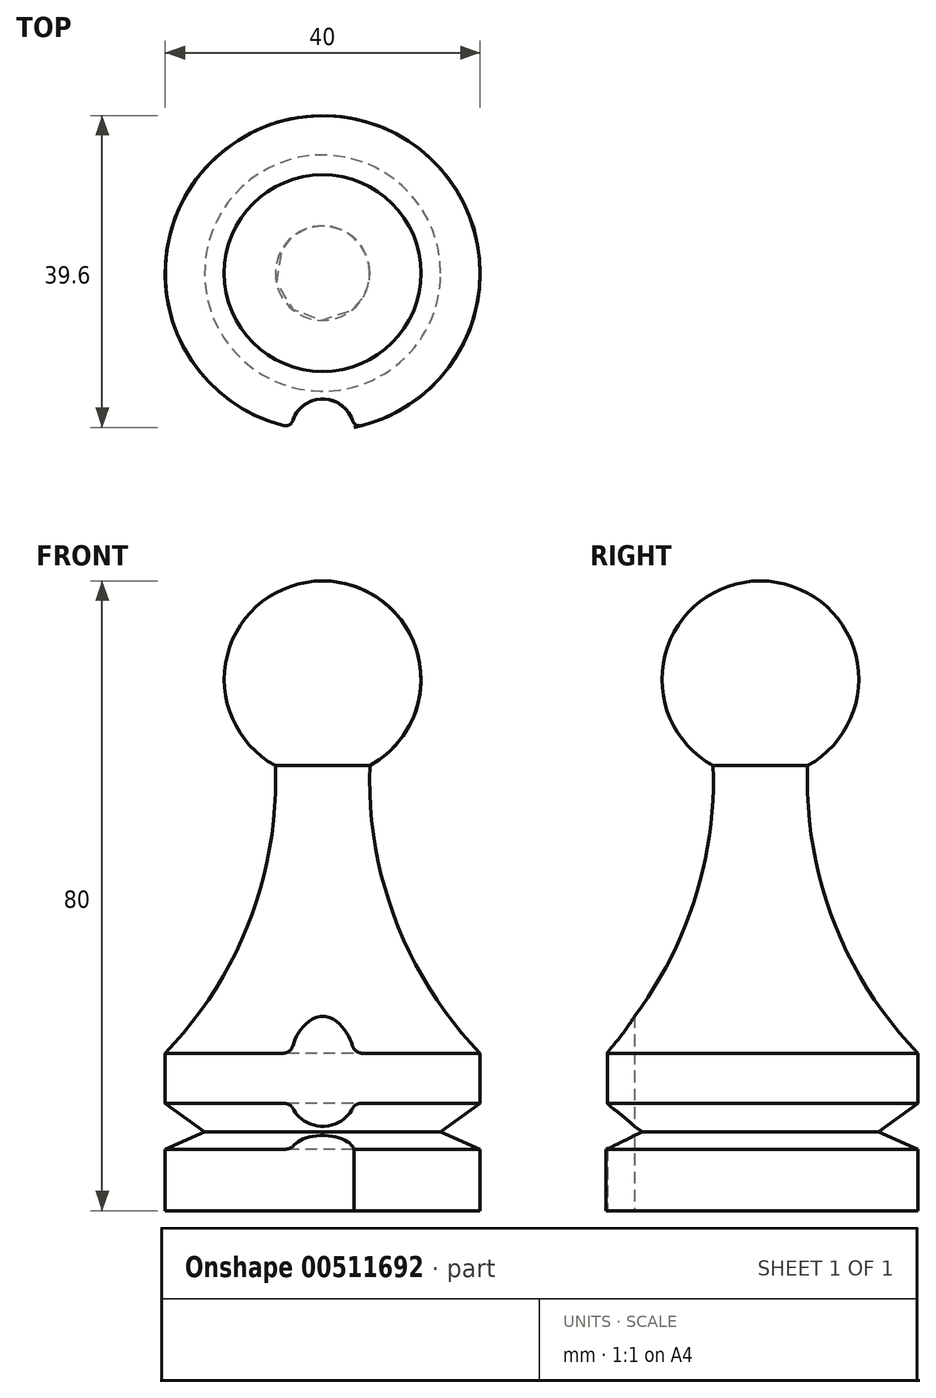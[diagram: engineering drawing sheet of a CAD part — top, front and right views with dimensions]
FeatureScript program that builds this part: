
annotation { "Feature Type Name" : "Feature", "Feature Type Description" : "" }
export const myFeature = defineFeature(function(context is Context, id is Id, definition is map)
    precondition{}
    {
        {
            var Q0;
            Q0=qCreatedBy(makeId("Front.planeOp"),FACE);
            var sketch = newSketch(context, id + "F0", { "sketchPlane" : qUnion([Q0])});
            skLineSegment(sketch, "E0", {"start": v(0, 53.24) * mm, "end": v(0, -26.76) * mm, "construction": true});
            skLineSegment(sketch, "E1", {"start": v(0, -26.76) * mm, "end": v(20, -26.76) * mm});
            skLineSegment(sketch, "E2", {"start": v(20, -26.76) * mm, "end": v(20, -18.97) * mm});
            skLineSegment(sketch, "E3", {"start": v(20, -18.97) * mm, "end": v(15, -16.76) * mm});
            skLineSegment(sketch, "E4", {"start": v(15, -16.76) * mm, "end": v(20, -13.11) * mm});
            skLineSegment(sketch, "E5", {"start": v(20, -13.11) * mm, "end": v(20, -6.76) * mm});
            skArc(sketch, "E6", {"start": v(6, 29.78) * mm, "mid": v(9.28, 10.08) * mm, "end": v(20, -6.76) * mm});
            skArc(sketch, "E7", {"start": v(6, 29.78) * mm, "mid": v(12.11, 43.84) * mm, "end": v(0, 53.24) * mm});
            skLineSegment(sketch, "E8", {"start": v(0, 53.24) * mm, "end": v(0, -26.76) * mm});
            skSolve(sketch);
        }
        {
            var Q0;
            Q0 = qSketchRegion(id + "F0", true);
            var Q1;
            Q1=sQuery(id+"F0.wireOp",EDGE,"E8");
            revolve(context, id + "F1", {"entities" : qUnion([Q0]), "axis" : qUnion([Q1]), "revolveType" : RevolveType.FULL});
        }
        {
            var Q0;
            Q0=makeQuery(id+"F1.opRevolve","SWEPT_FACE",FACE,{"disambiguationData":[OSD([sQuery(id+"F0.wireOp",EDGE,"E1")])]});
            var sketch = newSketch(context, id + "F2", { "sketchPlane" : qUnion([Q0])});
            skCircle(sketch, "E9", {"center": v(0, 20) * mm, "radius": 4 * mm});
            skSolve(sketch);
        }
        {
            var Q0;
            Q0 = qSketchRegion(id + "F2", true);
            extrude(context, id + "F3", {"entities" : qUnion([Q0]), "operationType" : NewBodyOperationType.REMOVE, "oppositeDirection" : true, "depth" : 25 * mm, "offsetDistance" : 25 * mm});
        }
        {
            var Q0;
            {var subQ0=sQuery(id+"F2.wireOp",EDGE,"E9");var subQ1=makeQuery(id+"F1.opRevolve","SWEPT_FACE",FACE,{"disambiguationData":[OSD([sQuery(id+"F0.wireOp",EDGE,"E4")])]});var subQ3=makeQuery(id+"F1.opRevolve","SWEPT_FACE",FACE,{"disambiguationData":[OSD([sQuery(id+"F0.wireOp",EDGE,"E5")])]});var subQ4=makeQuery(id+"F3.boolean.opBoolean","COPY",FACE,{"disambiguationData":[TD([subQ1])],"derivedFrom":makeQuery(id+"F3.opExtrude","SWEPT_FACE",FACE,{"disambiguationData":[OSD([subQ0])]})});Q0=makeQuery(id+"FM0jg12cZnN2cx2_1.5.F3.boolean.opBoolean","INTERSECT",EDGE,{"disambiguationData":[OD(0.0)],"derivedFrom":[makeQuery(id+"FM0jg12cZnN2cx2_1.4.F3.boolean.opBoolean","SPLIT",FACE,{"disambiguationData":[TD([subQ4])],"derivedFrom":makeQuery(id+"FM0jg12cZnN2cx2_1.3.F3.boolean.opBoolean","SPLIT",FACE,{"disambiguationData":[TD([subQ4])],"derivedFrom":makeQuery(id+"FM0jg12cZnN2cx2_1.2.F3.boolean.opBoolean","SPLIT",FACE,{"disambiguationData":[TD([subQ4])],"derivedFrom":makeQuery(id+"FM0jg12cZnN2cx2_1.1.F3.boolean.opBoolean","SPLIT",FACE,{"disambiguationData":[OD(1.0)],"derivedFrom":subQ3})})})}),makeQuery(id+"FM0jg12cZnN2cx2_1.5.F3.opExtrude","SWEPT_FACE",FACE,{"disambiguationData":[OSD([subQ0])]})]});}
            var Q1;
            {var subQ0=sQuery(id+"F2.wireOp",EDGE,"E9");var subQ1=makeQuery(id+"F1.opRevolve","SWEPT_FACE",FACE,{"disambiguationData":[OSD([sQuery(id+"F0.wireOp",EDGE,"E4")])]});var subQ3=makeQuery(id+"F1.opRevolve","SWEPT_FACE",FACE,{"disambiguationData":[OSD([sQuery(id+"F0.wireOp",EDGE,"E5")])]});var subQ4=makeQuery(id+"F3.boolean.opBoolean","COPY",FACE,{"disambiguationData":[TD([subQ1])],"derivedFrom":makeQuery(id+"F3.opExtrude","SWEPT_FACE",FACE,{"disambiguationData":[OSD([subQ0])]})});Q1=makeQuery(id+"FM0jg12cZnN2cx2_1.5.F3.boolean.opBoolean","INTERSECT",EDGE,{"disambiguationData":[OD(1.0)],"derivedFrom":[makeQuery(id+"FM0jg12cZnN2cx2_1.4.F3.boolean.opBoolean","SPLIT",FACE,{"disambiguationData":[TD([subQ4])],"derivedFrom":makeQuery(id+"FM0jg12cZnN2cx2_1.3.F3.boolean.opBoolean","SPLIT",FACE,{"disambiguationData":[TD([subQ4])],"derivedFrom":makeQuery(id+"FM0jg12cZnN2cx2_1.2.F3.boolean.opBoolean","SPLIT",FACE,{"disambiguationData":[TD([subQ4])],"derivedFrom":makeQuery(id+"FM0jg12cZnN2cx2_1.1.F3.boolean.opBoolean","SPLIT",FACE,{"disambiguationData":[OD(1.0)],"derivedFrom":subQ3})})})}),makeQuery(id+"FM0jg12cZnN2cx2_1.5.F3.opExtrude","SWEPT_FACE",FACE,{"disambiguationData":[OSD([subQ0])]})]});}
            var Q2;
            {var subQ0=sQuery(id+"F2.wireOp",EDGE,"E9");var subQ1=makeQuery(id+"F1.opRevolve","SWEPT_FACE",FACE,{"disambiguationData":[OSD([sQuery(id+"F0.wireOp",EDGE,"E1")])]});var subQ2=makeQuery(id+"F1.opRevolve","SWEPT_FACE",FACE,{"disambiguationData":[OSD([sQuery(id+"F0.wireOp",EDGE,"E2")])]});var subQ4=makeQuery(id+"F3.boolean.opBoolean","COPY",FACE,{"disambiguationData":[TD([subQ1])],"derivedFrom":makeQuery(id+"F3.opExtrude","SWEPT_FACE",FACE,{"disambiguationData":[OSD([subQ0])]})});Q2=makeQuery(id+"FM0jg12cZnN2cx2_1.5.F3.boolean.opBoolean","INTERSECT",EDGE,{"disambiguationData":[OD(0.0)],"derivedFrom":[makeQuery(id+"FM0jg12cZnN2cx2_1.4.F3.boolean.opBoolean","SPLIT",FACE,{"disambiguationData":[TD([subQ4])],"derivedFrom":makeQuery(id+"FM0jg12cZnN2cx2_1.3.F3.boolean.opBoolean","SPLIT",FACE,{"disambiguationData":[TD([subQ4])],"derivedFrom":makeQuery(id+"FM0jg12cZnN2cx2_1.2.F3.boolean.opBoolean","SPLIT",FACE,{"disambiguationData":[TD([subQ4])],"derivedFrom":makeQuery(id+"FM0jg12cZnN2cx2_1.1.F3.boolean.opBoolean","SPLIT",FACE,{"disambiguationData":[OD(1.0)],"derivedFrom":subQ2})})})}),makeQuery(id+"FM0jg12cZnN2cx2_1.5.F3.opExtrude","SWEPT_FACE",FACE,{"disambiguationData":[OSD([subQ0])]})]});}
            var Q3;
            {var subQ0=sQuery(id+"F2.wireOp",EDGE,"E9");var subQ1=makeQuery(id+"F1.opRevolve","SWEPT_FACE",FACE,{"disambiguationData":[OSD([sQuery(id+"F0.wireOp",EDGE,"E1")])]});var subQ2=makeQuery(id+"F1.opRevolve","SWEPT_FACE",FACE,{"disambiguationData":[OSD([sQuery(id+"F0.wireOp",EDGE,"E2")])]});var subQ4=makeQuery(id+"F3.boolean.opBoolean","COPY",FACE,{"disambiguationData":[TD([subQ1])],"derivedFrom":makeQuery(id+"F3.opExtrude","SWEPT_FACE",FACE,{"disambiguationData":[OSD([subQ0])]})});Q3=makeQuery(id+"FM0jg12cZnN2cx2_1.5.F3.boolean.opBoolean","INTERSECT",EDGE,{"disambiguationData":[OD(1.0)],"derivedFrom":[makeQuery(id+"FM0jg12cZnN2cx2_1.4.F3.boolean.opBoolean","SPLIT",FACE,{"disambiguationData":[TD([subQ4])],"derivedFrom":makeQuery(id+"FM0jg12cZnN2cx2_1.3.F3.boolean.opBoolean","SPLIT",FACE,{"disambiguationData":[TD([subQ4])],"derivedFrom":makeQuery(id+"FM0jg12cZnN2cx2_1.2.F3.boolean.opBoolean","SPLIT",FACE,{"disambiguationData":[TD([subQ4])],"derivedFrom":makeQuery(id+"FM0jg12cZnN2cx2_1.1.F3.boolean.opBoolean","SPLIT",FACE,{"disambiguationData":[OD(1.0)],"derivedFrom":subQ2})})})}),makeQuery(id+"FM0jg12cZnN2cx2_1.5.F3.opExtrude","SWEPT_FACE",FACE,{"disambiguationData":[OSD([subQ0])]})]});}
            var Q4;
            {var subQ0=sQuery(id+"F2.wireOp",EDGE,"E9");var subQ1=makeQuery(id+"F1.opRevolve","SWEPT_FACE",FACE,{"disambiguationData":[OSD([sQuery(id+"F0.wireOp",EDGE,"E4")])]});var subQ3=makeQuery(id+"F1.opRevolve","SWEPT_FACE",FACE,{"disambiguationData":[OSD([sQuery(id+"F0.wireOp",EDGE,"E5")])]});var subQ4=makeQuery(id+"F3.boolean.opBoolean","COPY",FACE,{"disambiguationData":[TD([subQ1])],"derivedFrom":makeQuery(id+"F3.opExtrude","SWEPT_FACE",FACE,{"disambiguationData":[OSD([subQ0])]})});Q4=makeQuery(id+"FM0jg12cZnN2cx2_1.4.F3.boolean.opBoolean","INTERSECT",EDGE,{"disambiguationData":[OD(0.0)],"derivedFrom":[makeQuery(id+"FM0jg12cZnN2cx2_1.3.F3.boolean.opBoolean","SPLIT",FACE,{"disambiguationData":[TD([subQ4])],"derivedFrom":makeQuery(id+"FM0jg12cZnN2cx2_1.2.F3.boolean.opBoolean","SPLIT",FACE,{"disambiguationData":[TD([subQ4])],"derivedFrom":makeQuery(id+"FM0jg12cZnN2cx2_1.1.F3.boolean.opBoolean","SPLIT",FACE,{"disambiguationData":[OD(1.0)],"derivedFrom":subQ3})})}),makeQuery(id+"FM0jg12cZnN2cx2_1.4.F3.opExtrude","SWEPT_FACE",FACE,{"disambiguationData":[OSD([subQ0])]})]});}
            var Q5;
            {var subQ0=sQuery(id+"F2.wireOp",EDGE,"E9");var subQ1=makeQuery(id+"F1.opRevolve","SWEPT_FACE",FACE,{"disambiguationData":[OSD([sQuery(id+"F0.wireOp",EDGE,"E4")])]});var subQ3=makeQuery(id+"F1.opRevolve","SWEPT_FACE",FACE,{"disambiguationData":[OSD([sQuery(id+"F0.wireOp",EDGE,"E5")])]});var subQ4=makeQuery(id+"F3.boolean.opBoolean","COPY",FACE,{"disambiguationData":[TD([subQ1])],"derivedFrom":makeQuery(id+"F3.opExtrude","SWEPT_FACE",FACE,{"disambiguationData":[OSD([subQ0])]})});Q5=makeQuery(id+"FM0jg12cZnN2cx2_1.4.F3.boolean.opBoolean","INTERSECT",EDGE,{"disambiguationData":[OD(1.0)],"derivedFrom":[makeQuery(id+"FM0jg12cZnN2cx2_1.3.F3.boolean.opBoolean","SPLIT",FACE,{"disambiguationData":[TD([subQ4])],"derivedFrom":makeQuery(id+"FM0jg12cZnN2cx2_1.2.F3.boolean.opBoolean","SPLIT",FACE,{"disambiguationData":[TD([subQ4])],"derivedFrom":makeQuery(id+"FM0jg12cZnN2cx2_1.1.F3.boolean.opBoolean","SPLIT",FACE,{"disambiguationData":[OD(1.0)],"derivedFrom":subQ3})})}),makeQuery(id+"FM0jg12cZnN2cx2_1.4.F3.opExtrude","SWEPT_FACE",FACE,{"disambiguationData":[OSD([subQ0])]})]});}
            var Q6;
            {var subQ0=sQuery(id+"F2.wireOp",EDGE,"E9");var subQ1=makeQuery(id+"F1.opRevolve","SWEPT_FACE",FACE,{"disambiguationData":[OSD([sQuery(id+"F0.wireOp",EDGE,"E1")])]});var subQ2=makeQuery(id+"F1.opRevolve","SWEPT_FACE",FACE,{"disambiguationData":[OSD([sQuery(id+"F0.wireOp",EDGE,"E2")])]});var subQ4=makeQuery(id+"F3.boolean.opBoolean","COPY",FACE,{"disambiguationData":[TD([subQ1])],"derivedFrom":makeQuery(id+"F3.opExtrude","SWEPT_FACE",FACE,{"disambiguationData":[OSD([subQ0])]})});Q6=makeQuery(id+"FM0jg12cZnN2cx2_1.4.F3.boolean.opBoolean","INTERSECT",EDGE,{"disambiguationData":[OD(0.0)],"derivedFrom":[makeQuery(id+"FM0jg12cZnN2cx2_1.3.F3.boolean.opBoolean","SPLIT",FACE,{"disambiguationData":[TD([subQ4])],"derivedFrom":makeQuery(id+"FM0jg12cZnN2cx2_1.2.F3.boolean.opBoolean","SPLIT",FACE,{"disambiguationData":[TD([subQ4])],"derivedFrom":makeQuery(id+"FM0jg12cZnN2cx2_1.1.F3.boolean.opBoolean","SPLIT",FACE,{"disambiguationData":[OD(1.0)],"derivedFrom":subQ2})})}),makeQuery(id+"FM0jg12cZnN2cx2_1.4.F3.opExtrude","SWEPT_FACE",FACE,{"disambiguationData":[OSD([subQ0])]})]});}
            var Q7;
            {var subQ0=sQuery(id+"F2.wireOp",EDGE,"E9");var subQ1=makeQuery(id+"F1.opRevolve","SWEPT_FACE",FACE,{"disambiguationData":[OSD([sQuery(id+"F0.wireOp",EDGE,"E1")])]});var subQ2=makeQuery(id+"F1.opRevolve","SWEPT_FACE",FACE,{"disambiguationData":[OSD([sQuery(id+"F0.wireOp",EDGE,"E2")])]});var subQ4=makeQuery(id+"F3.boolean.opBoolean","COPY",FACE,{"disambiguationData":[TD([subQ1])],"derivedFrom":makeQuery(id+"F3.opExtrude","SWEPT_FACE",FACE,{"disambiguationData":[OSD([subQ0])]})});Q7=makeQuery(id+"FM0jg12cZnN2cx2_1.4.F3.boolean.opBoolean","INTERSECT",EDGE,{"disambiguationData":[OD(1.0)],"derivedFrom":[makeQuery(id+"FM0jg12cZnN2cx2_1.3.F3.boolean.opBoolean","SPLIT",FACE,{"disambiguationData":[TD([subQ4])],"derivedFrom":makeQuery(id+"FM0jg12cZnN2cx2_1.2.F3.boolean.opBoolean","SPLIT",FACE,{"disambiguationData":[TD([subQ4])],"derivedFrom":makeQuery(id+"FM0jg12cZnN2cx2_1.1.F3.boolean.opBoolean","SPLIT",FACE,{"disambiguationData":[OD(1.0)],"derivedFrom":subQ2})})}),makeQuery(id+"FM0jg12cZnN2cx2_1.4.F3.opExtrude","SWEPT_FACE",FACE,{"disambiguationData":[OSD([subQ0])]})]});}
            var Q8;
            {var subQ0=sQuery(id+"F2.wireOp",EDGE,"E9");var subQ1=makeQuery(id+"F1.opRevolve","SWEPT_FACE",FACE,{"disambiguationData":[OSD([sQuery(id+"F0.wireOp",EDGE,"E4")])]});var subQ3=makeQuery(id+"F1.opRevolve","SWEPT_FACE",FACE,{"disambiguationData":[OSD([sQuery(id+"F0.wireOp",EDGE,"E5")])]});var subQ4=makeQuery(id+"F3.boolean.opBoolean","COPY",FACE,{"disambiguationData":[TD([subQ1])],"derivedFrom":makeQuery(id+"F3.opExtrude","SWEPT_FACE",FACE,{"disambiguationData":[OSD([subQ0])]})});Q8=makeQuery(id+"FM0jg12cZnN2cx2_1.6.F3.boolean.opBoolean","INTERSECT",EDGE,{"disambiguationData":[OD(0.0)],"derivedFrom":[makeQuery(id+"FM0jg12cZnN2cx2_1.5.F3.boolean.opBoolean","SPLIT",FACE,{"disambiguationData":[TD([subQ4])],"derivedFrom":makeQuery(id+"FM0jg12cZnN2cx2_1.4.F3.boolean.opBoolean","SPLIT",FACE,{"disambiguationData":[TD([subQ4])],"derivedFrom":makeQuery(id+"FM0jg12cZnN2cx2_1.3.F3.boolean.opBoolean","SPLIT",FACE,{"disambiguationData":[TD([subQ4])],"derivedFrom":makeQuery(id+"FM0jg12cZnN2cx2_1.2.F3.boolean.opBoolean","SPLIT",FACE,{"disambiguationData":[TD([subQ4])],"derivedFrom":makeQuery(id+"FM0jg12cZnN2cx2_1.1.F3.boolean.opBoolean","SPLIT",FACE,{"disambiguationData":[OD(1.0)],"derivedFrom":subQ3})})})})}),makeQuery(id+"FM0jg12cZnN2cx2_1.6.F3.opExtrude","SWEPT_FACE",FACE,{"disambiguationData":[OSD([subQ0])]})]});}
            var Q9;
            {var subQ0=sQuery(id+"F2.wireOp",EDGE,"E9");var subQ1=makeQuery(id+"F1.opRevolve","SWEPT_FACE",FACE,{"disambiguationData":[OSD([sQuery(id+"F0.wireOp",EDGE,"E4")])]});var subQ3=makeQuery(id+"F1.opRevolve","SWEPT_FACE",FACE,{"disambiguationData":[OSD([sQuery(id+"F0.wireOp",EDGE,"E5")])]});var subQ4=makeQuery(id+"F3.boolean.opBoolean","COPY",FACE,{"disambiguationData":[TD([subQ1])],"derivedFrom":makeQuery(id+"F3.opExtrude","SWEPT_FACE",FACE,{"disambiguationData":[OSD([subQ0])]})});Q9=makeQuery(id+"FM0jg12cZnN2cx2_1.6.F3.boolean.opBoolean","INTERSECT",EDGE,{"disambiguationData":[OD(1.0)],"derivedFrom":[makeQuery(id+"FM0jg12cZnN2cx2_1.5.F3.boolean.opBoolean","SPLIT",FACE,{"disambiguationData":[TD([subQ4])],"derivedFrom":makeQuery(id+"FM0jg12cZnN2cx2_1.4.F3.boolean.opBoolean","SPLIT",FACE,{"disambiguationData":[TD([subQ4])],"derivedFrom":makeQuery(id+"FM0jg12cZnN2cx2_1.3.F3.boolean.opBoolean","SPLIT",FACE,{"disambiguationData":[TD([subQ4])],"derivedFrom":makeQuery(id+"FM0jg12cZnN2cx2_1.2.F3.boolean.opBoolean","SPLIT",FACE,{"disambiguationData":[TD([subQ4])],"derivedFrom":makeQuery(id+"FM0jg12cZnN2cx2_1.1.F3.boolean.opBoolean","SPLIT",FACE,{"disambiguationData":[OD(1.0)],"derivedFrom":subQ3})})})})}),makeQuery(id+"FM0jg12cZnN2cx2_1.6.F3.opExtrude","SWEPT_FACE",FACE,{"disambiguationData":[OSD([subQ0])]})]});}
            var Q10;
            {var subQ0=sQuery(id+"F2.wireOp",EDGE,"E9");var subQ1=makeQuery(id+"F1.opRevolve","SWEPT_FACE",FACE,{"disambiguationData":[OSD([sQuery(id+"F0.wireOp",EDGE,"E1")])]});var subQ2=makeQuery(id+"F1.opRevolve","SWEPT_FACE",FACE,{"disambiguationData":[OSD([sQuery(id+"F0.wireOp",EDGE,"E2")])]});var subQ4=makeQuery(id+"F3.boolean.opBoolean","COPY",FACE,{"disambiguationData":[TD([subQ1])],"derivedFrom":makeQuery(id+"F3.opExtrude","SWEPT_FACE",FACE,{"disambiguationData":[OSD([subQ0])]})});Q10=makeQuery(id+"FM0jg12cZnN2cx2_1.6.F3.boolean.opBoolean","INTERSECT",EDGE,{"disambiguationData":[OD(0.0)],"derivedFrom":[makeQuery(id+"FM0jg12cZnN2cx2_1.5.F3.boolean.opBoolean","SPLIT",FACE,{"disambiguationData":[TD([subQ4])],"derivedFrom":makeQuery(id+"FM0jg12cZnN2cx2_1.4.F3.boolean.opBoolean","SPLIT",FACE,{"disambiguationData":[TD([subQ4])],"derivedFrom":makeQuery(id+"FM0jg12cZnN2cx2_1.3.F3.boolean.opBoolean","SPLIT",FACE,{"disambiguationData":[TD([subQ4])],"derivedFrom":makeQuery(id+"FM0jg12cZnN2cx2_1.2.F3.boolean.opBoolean","SPLIT",FACE,{"disambiguationData":[TD([subQ4])],"derivedFrom":makeQuery(id+"FM0jg12cZnN2cx2_1.1.F3.boolean.opBoolean","SPLIT",FACE,{"disambiguationData":[OD(1.0)],"derivedFrom":subQ2})})})})}),makeQuery(id+"FM0jg12cZnN2cx2_1.6.F3.opExtrude","SWEPT_FACE",FACE,{"disambiguationData":[OSD([subQ0])]})]});}
            var Q11;
            {var subQ0=sQuery(id+"F2.wireOp",EDGE,"E9");var subQ1=makeQuery(id+"F1.opRevolve","SWEPT_FACE",FACE,{"disambiguationData":[OSD([sQuery(id+"F0.wireOp",EDGE,"E1")])]});var subQ2=makeQuery(id+"F1.opRevolve","SWEPT_FACE",FACE,{"disambiguationData":[OSD([sQuery(id+"F0.wireOp",EDGE,"E2")])]});var subQ4=makeQuery(id+"F3.boolean.opBoolean","COPY",FACE,{"disambiguationData":[TD([subQ1])],"derivedFrom":makeQuery(id+"F3.opExtrude","SWEPT_FACE",FACE,{"disambiguationData":[OSD([subQ0])]})});Q11=makeQuery(id+"FM0jg12cZnN2cx2_1.6.F3.boolean.opBoolean","INTERSECT",EDGE,{"disambiguationData":[OD(1.0)],"derivedFrom":[makeQuery(id+"FM0jg12cZnN2cx2_1.5.F3.boolean.opBoolean","SPLIT",FACE,{"disambiguationData":[TD([subQ4])],"derivedFrom":makeQuery(id+"FM0jg12cZnN2cx2_1.4.F3.boolean.opBoolean","SPLIT",FACE,{"disambiguationData":[TD([subQ4])],"derivedFrom":makeQuery(id+"FM0jg12cZnN2cx2_1.3.F3.boolean.opBoolean","SPLIT",FACE,{"disambiguationData":[TD([subQ4])],"derivedFrom":makeQuery(id+"FM0jg12cZnN2cx2_1.2.F3.boolean.opBoolean","SPLIT",FACE,{"disambiguationData":[TD([subQ4])],"derivedFrom":makeQuery(id+"FM0jg12cZnN2cx2_1.1.F3.boolean.opBoolean","SPLIT",FACE,{"disambiguationData":[OD(1.0)],"derivedFrom":subQ2})})})})}),makeQuery(id+"FM0jg12cZnN2cx2_1.6.F3.opExtrude","SWEPT_FACE",FACE,{"disambiguationData":[OSD([subQ0])]})]});}
            var Q12;
            {var subQ0=sQuery(id+"F2.wireOp",EDGE,"E9");var subQ1=makeQuery(id+"F1.opRevolve","SWEPT_FACE",FACE,{"disambiguationData":[OSD([sQuery(id+"F0.wireOp",EDGE,"E4")])]});var subQ3=makeQuery(id+"F1.opRevolve","SWEPT_FACE",FACE,{"disambiguationData":[OSD([sQuery(id+"F0.wireOp",EDGE,"E5")])]});var subQ4=makeQuery(id+"F3.boolean.opBoolean","COPY",FACE,{"disambiguationData":[TD([subQ1])],"derivedFrom":makeQuery(id+"F3.opExtrude","SWEPT_FACE",FACE,{"disambiguationData":[OSD([subQ0])]})});Q12=makeQuery(id+"FM0jg12cZnN2cx2_1.7.F3.boolean.opBoolean","INTERSECT",EDGE,{"disambiguationData":[OD(0.0)],"derivedFrom":[makeQuery(id+"FM0jg12cZnN2cx2_1.6.F3.boolean.opBoolean","SPLIT",FACE,{"disambiguationData":[TD([subQ4])],"derivedFrom":makeQuery(id+"FM0jg12cZnN2cx2_1.5.F3.boolean.opBoolean","SPLIT",FACE,{"disambiguationData":[TD([subQ4])],"derivedFrom":makeQuery(id+"FM0jg12cZnN2cx2_1.4.F3.boolean.opBoolean","SPLIT",FACE,{"disambiguationData":[TD([subQ4])],"derivedFrom":makeQuery(id+"FM0jg12cZnN2cx2_1.3.F3.boolean.opBoolean","SPLIT",FACE,{"disambiguationData":[TD([subQ4])],"derivedFrom":makeQuery(id+"FM0jg12cZnN2cx2_1.2.F3.boolean.opBoolean","SPLIT",FACE,{"disambiguationData":[TD([subQ4])],"derivedFrom":makeQuery(id+"FM0jg12cZnN2cx2_1.1.F3.boolean.opBoolean","SPLIT",FACE,{"disambiguationData":[OD(1.0)],"derivedFrom":subQ3})})})})})}),makeQuery(id+"FM0jg12cZnN2cx2_1.7.F3.opExtrude","SWEPT_FACE",FACE,{"disambiguationData":[OSD([subQ0])]})]});}
            var Q13;
            {var subQ0=sQuery(id+"F2.wireOp",EDGE,"E9");var subQ1=makeQuery(id+"F1.opRevolve","SWEPT_FACE",FACE,{"disambiguationData":[OSD([sQuery(id+"F0.wireOp",EDGE,"E1")])]});var subQ2=makeQuery(id+"F1.opRevolve","SWEPT_FACE",FACE,{"disambiguationData":[OSD([sQuery(id+"F0.wireOp",EDGE,"E2")])]});var subQ4=makeQuery(id+"F3.boolean.opBoolean","COPY",FACE,{"disambiguationData":[TD([subQ1])],"derivedFrom":makeQuery(id+"F3.opExtrude","SWEPT_FACE",FACE,{"disambiguationData":[OSD([subQ0])]})});Q13=makeQuery(id+"FM0jg12cZnN2cx2_1.7.F3.boolean.opBoolean","INTERSECT",EDGE,{"disambiguationData":[OD(0.0)],"derivedFrom":[makeQuery(id+"FM0jg12cZnN2cx2_1.6.F3.boolean.opBoolean","SPLIT",FACE,{"disambiguationData":[TD([subQ4])],"derivedFrom":makeQuery(id+"FM0jg12cZnN2cx2_1.5.F3.boolean.opBoolean","SPLIT",FACE,{"disambiguationData":[TD([subQ4])],"derivedFrom":makeQuery(id+"FM0jg12cZnN2cx2_1.4.F3.boolean.opBoolean","SPLIT",FACE,{"disambiguationData":[TD([subQ4])],"derivedFrom":makeQuery(id+"FM0jg12cZnN2cx2_1.3.F3.boolean.opBoolean","SPLIT",FACE,{"disambiguationData":[TD([subQ4])],"derivedFrom":makeQuery(id+"FM0jg12cZnN2cx2_1.2.F3.boolean.opBoolean","SPLIT",FACE,{"disambiguationData":[TD([subQ4])],"derivedFrom":makeQuery(id+"FM0jg12cZnN2cx2_1.1.F3.boolean.opBoolean","SPLIT",FACE,{"disambiguationData":[OD(1.0)],"derivedFrom":subQ2})})})})})}),makeQuery(id+"FM0jg12cZnN2cx2_1.7.F3.opExtrude","SWEPT_FACE",FACE,{"disambiguationData":[OSD([subQ0])]})]});}
            var Q14;
            {var subQ0=sQuery(id+"F2.wireOp",EDGE,"E9");var subQ1=makeQuery(id+"F1.opRevolve","SWEPT_FACE",FACE,{"disambiguationData":[OSD([sQuery(id+"F0.wireOp",EDGE,"E4")])]});var subQ3=makeQuery(id+"F1.opRevolve","SWEPT_FACE",FACE,{"disambiguationData":[OSD([sQuery(id+"F0.wireOp",EDGE,"E5")])]});var subQ4=makeQuery(id+"F3.boolean.opBoolean","COPY",FACE,{"disambiguationData":[TD([subQ1])],"derivedFrom":makeQuery(id+"F3.opExtrude","SWEPT_FACE",FACE,{"disambiguationData":[OSD([subQ0])]})});Q14=makeQuery(id+"FM0jg12cZnN2cx2_1.7.F3.boolean.opBoolean","INTERSECT",EDGE,{"disambiguationData":[OD(1.0)],"derivedFrom":[makeQuery(id+"FM0jg12cZnN2cx2_1.6.F3.boolean.opBoolean","SPLIT",FACE,{"disambiguationData":[TD([subQ4])],"derivedFrom":makeQuery(id+"FM0jg12cZnN2cx2_1.5.F3.boolean.opBoolean","SPLIT",FACE,{"disambiguationData":[TD([subQ4])],"derivedFrom":makeQuery(id+"FM0jg12cZnN2cx2_1.4.F3.boolean.opBoolean","SPLIT",FACE,{"disambiguationData":[TD([subQ4])],"derivedFrom":makeQuery(id+"FM0jg12cZnN2cx2_1.3.F3.boolean.opBoolean","SPLIT",FACE,{"disambiguationData":[TD([subQ4])],"derivedFrom":makeQuery(id+"FM0jg12cZnN2cx2_1.2.F3.boolean.opBoolean","SPLIT",FACE,{"disambiguationData":[TD([subQ4])],"derivedFrom":makeQuery(id+"FM0jg12cZnN2cx2_1.1.F3.boolean.opBoolean","SPLIT",FACE,{"disambiguationData":[OD(1.0)],"derivedFrom":subQ3})})})})})}),makeQuery(id+"FM0jg12cZnN2cx2_1.7.F3.opExtrude","SWEPT_FACE",FACE,{"disambiguationData":[OSD([subQ0])]})]});}
            var Q15;
            {var subQ0=sQuery(id+"F2.wireOp",EDGE,"E9");var subQ1=makeQuery(id+"F1.opRevolve","SWEPT_FACE",FACE,{"disambiguationData":[OSD([sQuery(id+"F0.wireOp",EDGE,"E1")])]});var subQ2=makeQuery(id+"F1.opRevolve","SWEPT_FACE",FACE,{"disambiguationData":[OSD([sQuery(id+"F0.wireOp",EDGE,"E2")])]});var subQ4=makeQuery(id+"F3.boolean.opBoolean","COPY",FACE,{"disambiguationData":[TD([subQ1])],"derivedFrom":makeQuery(id+"F3.opExtrude","SWEPT_FACE",FACE,{"disambiguationData":[OSD([subQ0])]})});Q15=makeQuery(id+"FM0jg12cZnN2cx2_1.7.F3.boolean.opBoolean","INTERSECT",EDGE,{"disambiguationData":[OD(1.0)],"derivedFrom":[makeQuery(id+"FM0jg12cZnN2cx2_1.6.F3.boolean.opBoolean","SPLIT",FACE,{"disambiguationData":[TD([subQ4])],"derivedFrom":makeQuery(id+"FM0jg12cZnN2cx2_1.5.F3.boolean.opBoolean","SPLIT",FACE,{"disambiguationData":[TD([subQ4])],"derivedFrom":makeQuery(id+"FM0jg12cZnN2cx2_1.4.F3.boolean.opBoolean","SPLIT",FACE,{"disambiguationData":[TD([subQ4])],"derivedFrom":makeQuery(id+"FM0jg12cZnN2cx2_1.3.F3.boolean.opBoolean","SPLIT",FACE,{"disambiguationData":[TD([subQ4])],"derivedFrom":makeQuery(id+"FM0jg12cZnN2cx2_1.2.F3.boolean.opBoolean","SPLIT",FACE,{"disambiguationData":[TD([subQ4])],"derivedFrom":makeQuery(id+"FM0jg12cZnN2cx2_1.1.F3.boolean.opBoolean","SPLIT",FACE,{"disambiguationData":[OD(1.0)],"derivedFrom":subQ2})})})})})}),makeQuery(id+"FM0jg12cZnN2cx2_1.7.F3.opExtrude","SWEPT_FACE",FACE,{"disambiguationData":[OSD([subQ0])]})]});}
            var Q16;
            Q16=makeQuery(id+"F3.boolean.opBoolean","INTERSECT",EDGE,{"disambiguationData":[OD(0.0)],"derivedFrom":[makeQuery(id+"F1.opRevolve","SWEPT_FACE",FACE,{"disambiguationData":[OSD([sQuery(id+"F0.wireOp",EDGE,"E5")])]}),makeQuery(id+"F3.opExtrude","SWEPT_FACE",FACE,{"disambiguationData":[OSD([sQuery(id+"F2.wireOp",EDGE,"E9")])]})]});
            var Q17;
            Q17=makeQuery(id+"F3.boolean.opBoolean","INTERSECT",EDGE,{"disambiguationData":[OD(0.0)],"derivedFrom":[makeQuery(id+"F1.opRevolve","SWEPT_FACE",FACE,{"disambiguationData":[OSD([sQuery(id+"F0.wireOp",EDGE,"E2")])]}),makeQuery(id+"F3.opExtrude","SWEPT_FACE",FACE,{"disambiguationData":[OSD([sQuery(id+"F2.wireOp",EDGE,"E9")])]})]});
            var Q18;
            Q18=makeQuery(id+"F3.boolean.opBoolean","INTERSECT",EDGE,{"disambiguationData":[OD(1.0)],"derivedFrom":[makeQuery(id+"F1.opRevolve","SWEPT_FACE",FACE,{"disambiguationData":[OSD([sQuery(id+"F0.wireOp",EDGE,"E5")])]}),makeQuery(id+"F3.opExtrude","SWEPT_FACE",FACE,{"disambiguationData":[OSD([sQuery(id+"F2.wireOp",EDGE,"E9")])]})]});
            var Q19;
            Q19=makeQuery(id+"FM0jg12cZnN2cx2_1.1.F3.boolean.opBoolean","INTERSECT",EDGE,{"disambiguationData":[OD(1.0)],"derivedFrom":[makeQuery(id+"F1.opRevolve","SWEPT_FACE",FACE,{"disambiguationData":[OSD([sQuery(id+"F0.wireOp",EDGE,"E5")])]}),makeQuery(id+"FM0jg12cZnN2cx2_1.1.F3.opExtrude","SWEPT_FACE",FACE,{"disambiguationData":[OSD([sQuery(id+"F2.wireOp",EDGE,"E9")])]})]});
            var Q20;
            Q20=makeQuery(id+"FM0jg12cZnN2cx2_1.1.F3.boolean.opBoolean","INTERSECT",EDGE,{"disambiguationData":[OD(1.0)],"derivedFrom":[makeQuery(id+"F1.opRevolve","SWEPT_FACE",FACE,{"disambiguationData":[OSD([sQuery(id+"F0.wireOp",EDGE,"E2")])]}),makeQuery(id+"FM0jg12cZnN2cx2_1.1.F3.opExtrude","SWEPT_FACE",FACE,{"disambiguationData":[OSD([sQuery(id+"F2.wireOp",EDGE,"E9")])]})]});
            var Q21;
            Q21=makeQuery(id+"FM0jg12cZnN2cx2_1.1.F3.boolean.opBoolean","INTERSECT",EDGE,{"disambiguationData":[OD(0.0)],"derivedFrom":[makeQuery(id+"F1.opRevolve","SWEPT_FACE",FACE,{"disambiguationData":[OSD([sQuery(id+"F0.wireOp",EDGE,"E5")])]}),makeQuery(id+"FM0jg12cZnN2cx2_1.1.F3.opExtrude","SWEPT_FACE",FACE,{"disambiguationData":[OSD([sQuery(id+"F2.wireOp",EDGE,"E9")])]})]});
            var Q22;
            Q22=makeQuery(id+"FM0jg12cZnN2cx2_1.1.F3.boolean.opBoolean","INTERSECT",EDGE,{"disambiguationData":[OD(0.0)],"derivedFrom":[makeQuery(id+"F1.opRevolve","SWEPT_FACE",FACE,{"disambiguationData":[OSD([sQuery(id+"F0.wireOp",EDGE,"E2")])]}),makeQuery(id+"FM0jg12cZnN2cx2_1.1.F3.opExtrude","SWEPT_FACE",FACE,{"disambiguationData":[OSD([sQuery(id+"F2.wireOp",EDGE,"E9")])]})]});
            var Q23;
            Q23=makeQuery(id+"FM0jg12cZnN2cx2_1.2.F3.boolean.opBoolean","INTERSECT",EDGE,{"disambiguationData":[OD(0.0)],"derivedFrom":[makeQuery(id+"FM0jg12cZnN2cx2_1.1.F3.boolean.opBoolean","SPLIT",FACE,{"disambiguationData":[OD(1.0)],"derivedFrom":makeQuery(id+"F1.opRevolve","SWEPT_FACE",FACE,{"disambiguationData":[OSD([sQuery(id+"F0.wireOp",EDGE,"E5")])]})}),makeQuery(id+"FM0jg12cZnN2cx2_1.2.F3.opExtrude","SWEPT_FACE",FACE,{"disambiguationData":[OSD([sQuery(id+"F2.wireOp",EDGE,"E9")])]})]});
            var Q24;
            Q24=makeQuery(id+"FM0jg12cZnN2cx2_1.2.F3.boolean.opBoolean","INTERSECT",EDGE,{"disambiguationData":[OD(0.0)],"derivedFrom":[makeQuery(id+"FM0jg12cZnN2cx2_1.1.F3.boolean.opBoolean","SPLIT",FACE,{"disambiguationData":[OD(1.0)],"derivedFrom":makeQuery(id+"F1.opRevolve","SWEPT_FACE",FACE,{"disambiguationData":[OSD([sQuery(id+"F0.wireOp",EDGE,"E2")])]})}),makeQuery(id+"FM0jg12cZnN2cx2_1.2.F3.opExtrude","SWEPT_FACE",FACE,{"disambiguationData":[OSD([sQuery(id+"F2.wireOp",EDGE,"E9")])]})]});
            var Q25;
            Q25=makeQuery(id+"FM0jg12cZnN2cx2_1.2.F3.boolean.opBoolean","INTERSECT",EDGE,{"disambiguationData":[OD(1.0)],"derivedFrom":[makeQuery(id+"FM0jg12cZnN2cx2_1.1.F3.boolean.opBoolean","SPLIT",FACE,{"disambiguationData":[OD(1.0)],"derivedFrom":makeQuery(id+"F1.opRevolve","SWEPT_FACE",FACE,{"disambiguationData":[OSD([sQuery(id+"F0.wireOp",EDGE,"E5")])]})}),makeQuery(id+"FM0jg12cZnN2cx2_1.2.F3.opExtrude","SWEPT_FACE",FACE,{"disambiguationData":[OSD([sQuery(id+"F2.wireOp",EDGE,"E9")])]})]});
            var Q26;
            Q26=makeQuery(id+"FM0jg12cZnN2cx2_1.2.F3.boolean.opBoolean","INTERSECT",EDGE,{"disambiguationData":[OD(1.0)],"derivedFrom":[makeQuery(id+"FM0jg12cZnN2cx2_1.1.F3.boolean.opBoolean","SPLIT",FACE,{"disambiguationData":[OD(1.0)],"derivedFrom":makeQuery(id+"F1.opRevolve","SWEPT_FACE",FACE,{"disambiguationData":[OSD([sQuery(id+"F0.wireOp",EDGE,"E2")])]})}),makeQuery(id+"FM0jg12cZnN2cx2_1.2.F3.opExtrude","SWEPT_FACE",FACE,{"disambiguationData":[OSD([sQuery(id+"F2.wireOp",EDGE,"E9")])]})]});
            var Q27;
            {var subQ0=sQuery(id+"F2.wireOp",EDGE,"E9");var subQ1=makeQuery(id+"F1.opRevolve","SWEPT_FACE",FACE,{"disambiguationData":[OSD([sQuery(id+"F0.wireOp",EDGE,"E4")])]});var subQ3=makeQuery(id+"F1.opRevolve","SWEPT_FACE",FACE,{"disambiguationData":[OSD([sQuery(id+"F0.wireOp",EDGE,"E5")])]});Q27=makeQuery(id+"FM0jg12cZnN2cx2_1.3.F3.boolean.opBoolean","INTERSECT",EDGE,{"disambiguationData":[OD(0.0)],"derivedFrom":[makeQuery(id+"FM0jg12cZnN2cx2_1.2.F3.boolean.opBoolean","SPLIT",FACE,{"disambiguationData":[TD([makeQuery(id+"F3.boolean.opBoolean","COPY",FACE,{"disambiguationData":[TD([subQ1])],"derivedFrom":makeQuery(id+"F3.opExtrude","SWEPT_FACE",FACE,{"disambiguationData":[OSD([subQ0])]})})])],"derivedFrom":makeQuery(id+"FM0jg12cZnN2cx2_1.1.F3.boolean.opBoolean","SPLIT",FACE,{"disambiguationData":[OD(1.0)],"derivedFrom":subQ3})}),makeQuery(id+"FM0jg12cZnN2cx2_1.3.F3.opExtrude","SWEPT_FACE",FACE,{"disambiguationData":[OSD([subQ0])]})]});}
            var Q28;
            {var subQ0=sQuery(id+"F2.wireOp",EDGE,"E9");var subQ1=makeQuery(id+"F1.opRevolve","SWEPT_FACE",FACE,{"disambiguationData":[OSD([sQuery(id+"F0.wireOp",EDGE,"E1")])]});var subQ2=makeQuery(id+"F1.opRevolve","SWEPT_FACE",FACE,{"disambiguationData":[OSD([sQuery(id+"F0.wireOp",EDGE,"E2")])]});Q28=makeQuery(id+"FM0jg12cZnN2cx2_1.3.F3.boolean.opBoolean","INTERSECT",EDGE,{"disambiguationData":[OD(0.0)],"derivedFrom":[makeQuery(id+"FM0jg12cZnN2cx2_1.2.F3.boolean.opBoolean","SPLIT",FACE,{"disambiguationData":[TD([makeQuery(id+"F3.boolean.opBoolean","COPY",FACE,{"disambiguationData":[TD([subQ1])],"derivedFrom":makeQuery(id+"F3.opExtrude","SWEPT_FACE",FACE,{"disambiguationData":[OSD([subQ0])]})})])],"derivedFrom":makeQuery(id+"FM0jg12cZnN2cx2_1.1.F3.boolean.opBoolean","SPLIT",FACE,{"disambiguationData":[OD(1.0)],"derivedFrom":subQ2})}),makeQuery(id+"FM0jg12cZnN2cx2_1.3.F3.opExtrude","SWEPT_FACE",FACE,{"disambiguationData":[OSD([subQ0])]})]});}
            var Q29;
            {var subQ0=sQuery(id+"F2.wireOp",EDGE,"E9");var subQ1=makeQuery(id+"F1.opRevolve","SWEPT_FACE",FACE,{"disambiguationData":[OSD([sQuery(id+"F0.wireOp",EDGE,"E4")])]});var subQ3=makeQuery(id+"F1.opRevolve","SWEPT_FACE",FACE,{"disambiguationData":[OSD([sQuery(id+"F0.wireOp",EDGE,"E5")])]});Q29=makeQuery(id+"FM0jg12cZnN2cx2_1.3.F3.boolean.opBoolean","INTERSECT",EDGE,{"disambiguationData":[OD(1.0)],"derivedFrom":[makeQuery(id+"FM0jg12cZnN2cx2_1.2.F3.boolean.opBoolean","SPLIT",FACE,{"disambiguationData":[TD([makeQuery(id+"F3.boolean.opBoolean","COPY",FACE,{"disambiguationData":[TD([subQ1])],"derivedFrom":makeQuery(id+"F3.opExtrude","SWEPT_FACE",FACE,{"disambiguationData":[OSD([subQ0])]})})])],"derivedFrom":makeQuery(id+"FM0jg12cZnN2cx2_1.1.F3.boolean.opBoolean","SPLIT",FACE,{"disambiguationData":[OD(1.0)],"derivedFrom":subQ3})}),makeQuery(id+"FM0jg12cZnN2cx2_1.3.F3.opExtrude","SWEPT_FACE",FACE,{"disambiguationData":[OSD([subQ0])]})]});}
            var Q30;
            {var subQ0=sQuery(id+"F2.wireOp",EDGE,"E9");var subQ1=makeQuery(id+"F1.opRevolve","SWEPT_FACE",FACE,{"disambiguationData":[OSD([sQuery(id+"F0.wireOp",EDGE,"E1")])]});var subQ2=makeQuery(id+"F1.opRevolve","SWEPT_FACE",FACE,{"disambiguationData":[OSD([sQuery(id+"F0.wireOp",EDGE,"E2")])]});Q30=makeQuery(id+"FM0jg12cZnN2cx2_1.3.F3.boolean.opBoolean","INTERSECT",EDGE,{"disambiguationData":[OD(1.0)],"derivedFrom":[makeQuery(id+"FM0jg12cZnN2cx2_1.2.F3.boolean.opBoolean","SPLIT",FACE,{"disambiguationData":[TD([makeQuery(id+"F3.boolean.opBoolean","COPY",FACE,{"disambiguationData":[TD([subQ1])],"derivedFrom":makeQuery(id+"F3.opExtrude","SWEPT_FACE",FACE,{"disambiguationData":[OSD([subQ0])]})})])],"derivedFrom":makeQuery(id+"FM0jg12cZnN2cx2_1.1.F3.boolean.opBoolean","SPLIT",FACE,{"disambiguationData":[OD(1.0)],"derivedFrom":subQ2})}),makeQuery(id+"FM0jg12cZnN2cx2_1.3.F3.opExtrude","SWEPT_FACE",FACE,{"disambiguationData":[OSD([subQ0])]})]});}
            fillet(context, id + "F4", {"entities" : qUnion([Q0, Q1, Q2, Q3, Q4, Q5, Q6, Q7, Q8, Q9, Q10, Q11, Q12, Q13, Q14, Q15, Q16, Q17, Q18, Q19, Q20, Q21, Q22, Q23, Q24, Q25, Q26, Q27, Q28, Q29, Q30]), "radius" : 1 * mm, "tangentPropagation" : true, "allowEdgeOverflow" : false});
        }
    });
